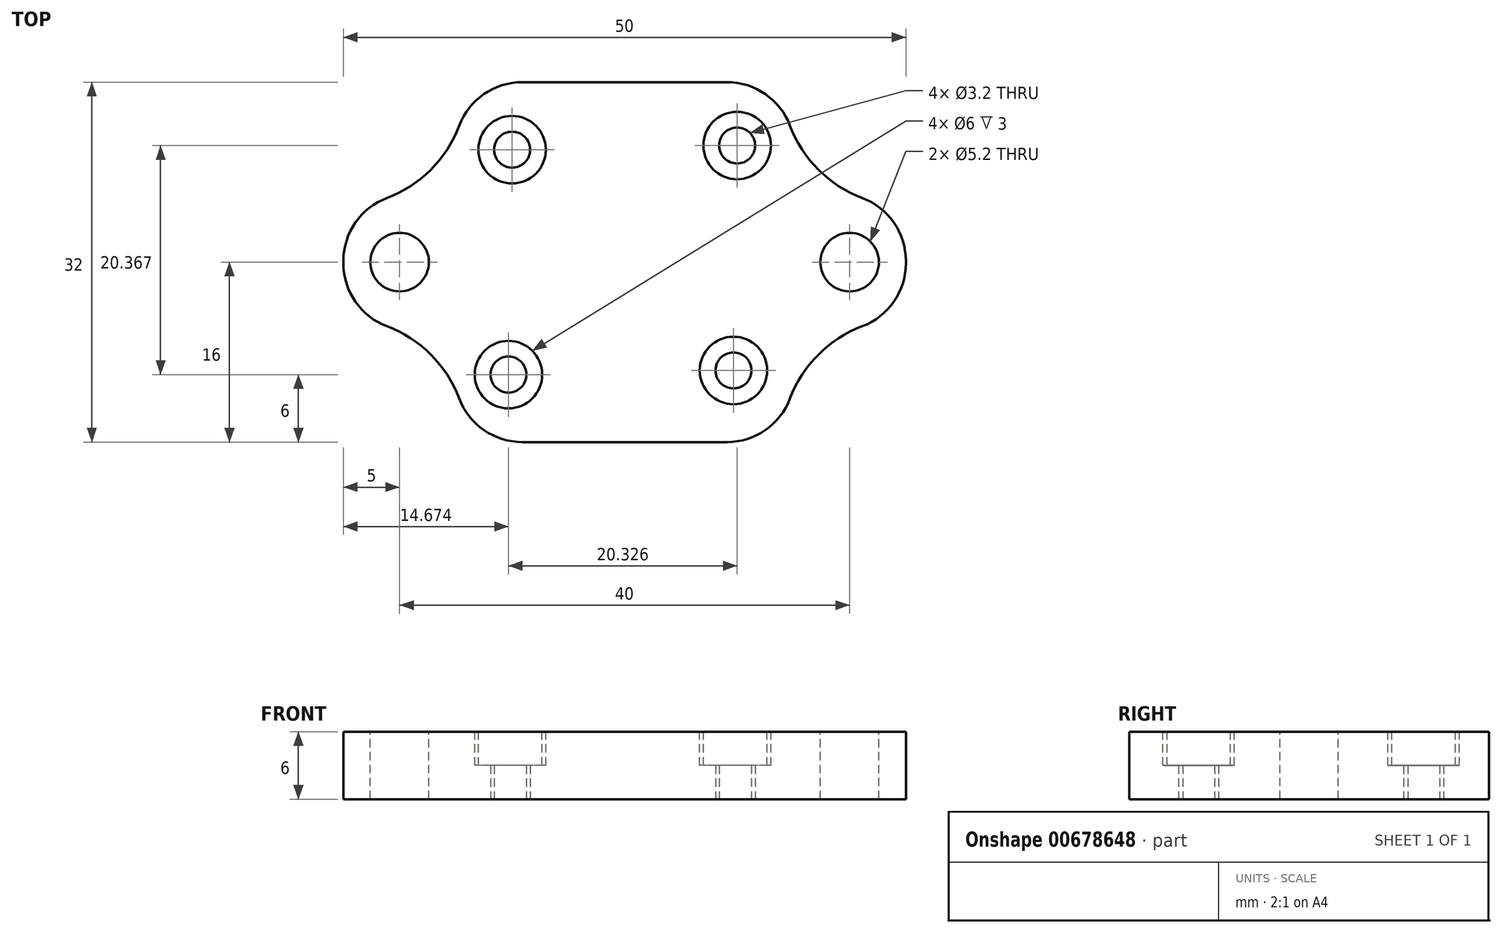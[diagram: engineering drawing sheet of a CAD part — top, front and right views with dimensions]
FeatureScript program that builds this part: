
annotation { "Feature Type Name" : "Feature", "Feature Type Description" : "" }
export const myFeature = defineFeature(function(context is Context, id is Id, definition is map)
    precondition{}
    {
        {
            var Q0;
            Q0=qCreatedBy(makeId("Top.planeOp"),FACE);
            var sketch = newSketch(context, id + "F0", { "sketchPlane" : qUnion([Q0])});
            skCircle(sketch, "E0", {"center": v(-10, 10) * mm, "radius": 1.6 * mm});
            skCircle(sketch, "E1", {"center": v(10, 10.37) * mm, "radius": 1.6 * mm});
            skCircle(sketch, "E2", {"center": v(-10.33, -10) * mm, "radius": 1.6 * mm});
            skCircle(sketch, "E3", {"center": v(9.67, -9.63) * mm, "radius": 1.6 * mm});
            skLineSegment(sketch, "E4.bottom", {"start": v(-25, 16) * mm, "end": v(25, 16) * mm});
            skLineSegment(sketch, "E4.top", {"start": v(-25, -16) * mm, "end": v(25, -16) * mm});
            skLineSegment(sketch, "E4.left", {"start": v(-25, 16) * mm, "end": v(-25, -16) * mm});
            skLineSegment(sketch, "E4.right", {"start": v(25, 16) * mm, "end": v(25, -16) * mm});
            skPoint(sketch, "E4.middle", {"position": v(0, 0) * mm});
            skSolve(sketch);
        }
        {
            var Q0;
            Q0 = qSketchRegion(id + "F0", true);
            extrude(context, id + "F1", {"entities" : qUnion([Q0]), "depth" : 6 * mm, "offsetDistance" : 25.4 * mm});
        }
        {
            var Q0;
            Q0=makeQuery(id+"F1.opExtrude","CAP_FACE",FACE,{"disambiguationData":[OSD([sQuery(id+"F0.wireOp",EDGE,"E0"),sQuery(id+"F0.wireOp",EDGE,"E1"),sQuery(id+"F0.wireOp",EDGE,"E2"),sQuery(id+"F0.wireOp",EDGE,"E3"),sQuery(id+"F0.wireOp",EDGE,"E4.bottom"),sQuery(id+"F0.wireOp",EDGE,"E4.top"),sQuery(id+"F0.wireOp",EDGE,"E4.left"),sQuery(id+"F0.wireOp",EDGE,"E4.right")])],"isStart":false});
            var sketch = newSketch(context, id + "F2", { "sketchPlane" : qUnion([Q0])});
            skCircle(sketch, "E5", {"center": v(-10, 10) * mm, "radius": 3 * mm});
            skCircle(sketch, "E6", {"center": v(-10.33, -10) * mm, "radius": 3 * mm});
            skCircle(sketch, "E7", {"center": v(9.67, -9.63) * mm, "radius": 3 * mm});
            skCircle(sketch, "E8", {"center": v(10, 10.37) * mm, "radius": 3 * mm});
            skSolve(sketch);
        }
        {
            var Q0;
            Q0 = qSketchRegion(id + "F2", true);
            extrude(context, id + "F3", {"entities" : qUnion([Q0]), "operationType" : NewBodyOperationType.REMOVE, "oppositeDirection" : true, "depth" : 3 * mm, "offsetDistance" : 25.4 * mm});
        }
        {
            var Q0;
            Q0=makeQuery(id+"F1.opExtrude","CAP_FACE",FACE,{"disambiguationData":[OSD([sQuery(id+"F0.wireOp",EDGE,"E0"),sQuery(id+"F0.wireOp",EDGE,"E1"),sQuery(id+"F0.wireOp",EDGE,"E2"),sQuery(id+"F0.wireOp",EDGE,"E3"),sQuery(id+"F0.wireOp",EDGE,"E4.bottom"),sQuery(id+"F0.wireOp",EDGE,"E4.top"),sQuery(id+"F0.wireOp",EDGE,"E4.left"),sQuery(id+"F0.wireOp",EDGE,"E4.right")])],"isStart":false});
            var sketch = newSketch(context, id + "F4", { "sketchPlane" : qUnion([Q0])});
            skCircle(sketch, "E9", {"center": v(-20, 0) * mm, "radius": 2.6 * mm});
            skCircle(sketch, "E10", {"center": v(20, 0) * mm, "radius": 2.6 * mm});
            skSolve(sketch);
        }
        {
            var Q0;
            Q0 = qSketchRegion(id + "F4", true);
            extrude(context, id + "F5", {"entities" : qUnion([Q0]), "operationType" : NewBodyOperationType.REMOVE, "oppositeDirection" : true, "depth" : 25.4 * mm, "offsetDistance" : 25.4 * mm});
        }
        {
            var Q0;
            Q0=makeQuery(id+"F1.opExtrude","CAP_FACE",FACE,{"disambiguationData":[OSD([sQuery(id+"F0.wireOp",EDGE,"E0"),sQuery(id+"F0.wireOp",EDGE,"E1"),sQuery(id+"F0.wireOp",EDGE,"E2"),sQuery(id+"F0.wireOp",EDGE,"E3"),sQuery(id+"F0.wireOp",EDGE,"E4.bottom"),sQuery(id+"F0.wireOp",EDGE,"E4.top"),sQuery(id+"F0.wireOp",EDGE,"E4.left"),sQuery(id+"F0.wireOp",EDGE,"E4.right")])],"isStart":false});
            var sketch = newSketch(context, id + "F6", { "sketchPlane" : qUnion([Q0])});
            skCircle(sketch, "E11", {"center": v(-25, 16) * mm, "radius": 11 * mm});
            skCircle(sketch, "E12", {"center": v(25, 16) * mm, "radius": 11 * mm});
            skCircle(sketch, "E13", {"center": v(25, -16) * mm, "radius": 11 * mm});
            skCircle(sketch, "E14", {"center": v(-25, -16) * mm, "radius": 11 * mm});
            skSolve(sketch);
        }
        {
            var Q0;
            Q0 = qSketchRegion(id + "F6", true);
            extrude(context, id + "F7", {"entities" : qUnion([Q0]), "operationType" : NewBodyOperationType.REMOVE, "oppositeDirection" : true, "depth" : 25.4 * mm, "offsetDistance" : 25.4 * mm});
        }
        {
            var Q0;
            Q0=makeQuery(id+"F7.boolean.opBoolean","INTERSECT",EDGE,{"derivedFrom":[makeQuery(id+"F1.opExtrude","SWEPT_FACE",FACE,{"disambiguationData":[OSD([sQuery(id+"F0.wireOp",EDGE,"E4.top")])]}),makeQuery(id+"F7.opExtrude","SWEPT_FACE",FACE,{"disambiguationData":[OSD([sQuery(id+"F6.wireOp",EDGE,"E14")])]})]});
            var Q1;
            Q1=makeQuery(id+"F7.boolean.opBoolean","INTERSECT",EDGE,{"derivedFrom":[makeQuery(id+"F1.opExtrude","SWEPT_FACE",FACE,{"disambiguationData":[OSD([sQuery(id+"F0.wireOp",EDGE,"E4.left")])]}),makeQuery(id+"F7.opExtrude","SWEPT_FACE",FACE,{"disambiguationData":[OSD([sQuery(id+"F6.wireOp",EDGE,"E14")])]})]});
            var Q2;
            Q2=makeQuery(id+"F7.boolean.opBoolean","INTERSECT",EDGE,{"derivedFrom":[makeQuery(id+"F1.opExtrude","SWEPT_FACE",FACE,{"disambiguationData":[OSD([sQuery(id+"F0.wireOp",EDGE,"E4.top")])]}),makeQuery(id+"F7.opExtrude","SWEPT_FACE",FACE,{"disambiguationData":[OSD([sQuery(id+"F6.wireOp",EDGE,"E13")])]})]});
            var Q3;
            Q3=makeQuery(id+"F7.boolean.opBoolean","INTERSECT",EDGE,{"derivedFrom":[makeQuery(id+"F1.opExtrude","SWEPT_FACE",FACE,{"disambiguationData":[OSD([sQuery(id+"F0.wireOp",EDGE,"E4.right")])]}),makeQuery(id+"F7.opExtrude","SWEPT_FACE",FACE,{"disambiguationData":[OSD([sQuery(id+"F6.wireOp",EDGE,"E13")])]})]});
            var Q4;
            Q4=makeQuery(id+"F7.boolean.opBoolean","INTERSECT",EDGE,{"derivedFrom":[makeQuery(id+"F1.opExtrude","SWEPT_FACE",FACE,{"disambiguationData":[OSD([sQuery(id+"F0.wireOp",EDGE,"E4.right")])]}),makeQuery(id+"F7.opExtrude","SWEPT_FACE",FACE,{"disambiguationData":[OSD([sQuery(id+"F6.wireOp",EDGE,"E12")])]})]});
            var Q5;
            Q5=makeQuery(id+"F7.boolean.opBoolean","INTERSECT",EDGE,{"derivedFrom":[makeQuery(id+"F1.opExtrude","SWEPT_FACE",FACE,{"disambiguationData":[OSD([sQuery(id+"F0.wireOp",EDGE,"E4.bottom")])]}),makeQuery(id+"F7.opExtrude","SWEPT_FACE",FACE,{"disambiguationData":[OSD([sQuery(id+"F6.wireOp",EDGE,"E12")])]})]});
            var Q6;
            Q6=makeQuery(id+"F7.boolean.opBoolean","INTERSECT",EDGE,{"derivedFrom":[makeQuery(id+"F1.opExtrude","SWEPT_FACE",FACE,{"disambiguationData":[OSD([sQuery(id+"F0.wireOp",EDGE,"E4.bottom")])]}),makeQuery(id+"F7.opExtrude","SWEPT_FACE",FACE,{"disambiguationData":[OSD([sQuery(id+"F6.wireOp",EDGE,"E11")])]})]});
            var Q7;
            Q7=makeQuery(id+"F7.boolean.opBoolean","INTERSECT",EDGE,{"derivedFrom":[makeQuery(id+"F1.opExtrude","SWEPT_FACE",FACE,{"disambiguationData":[OSD([sQuery(id+"F0.wireOp",EDGE,"E4.left")])]}),makeQuery(id+"F7.opExtrude","SWEPT_FACE",FACE,{"disambiguationData":[OSD([sQuery(id+"F6.wireOp",EDGE,"E11")])]})]});
            fillet(context, id + "F8", {"entities" : qUnion([Q0, Q1, Q2, Q3, Q4, Q5, Q6, Q7]), "radius" : 6 * mm, "tangentPropagation" : true, "allowEdgeOverflow" : false});
        }
    });
